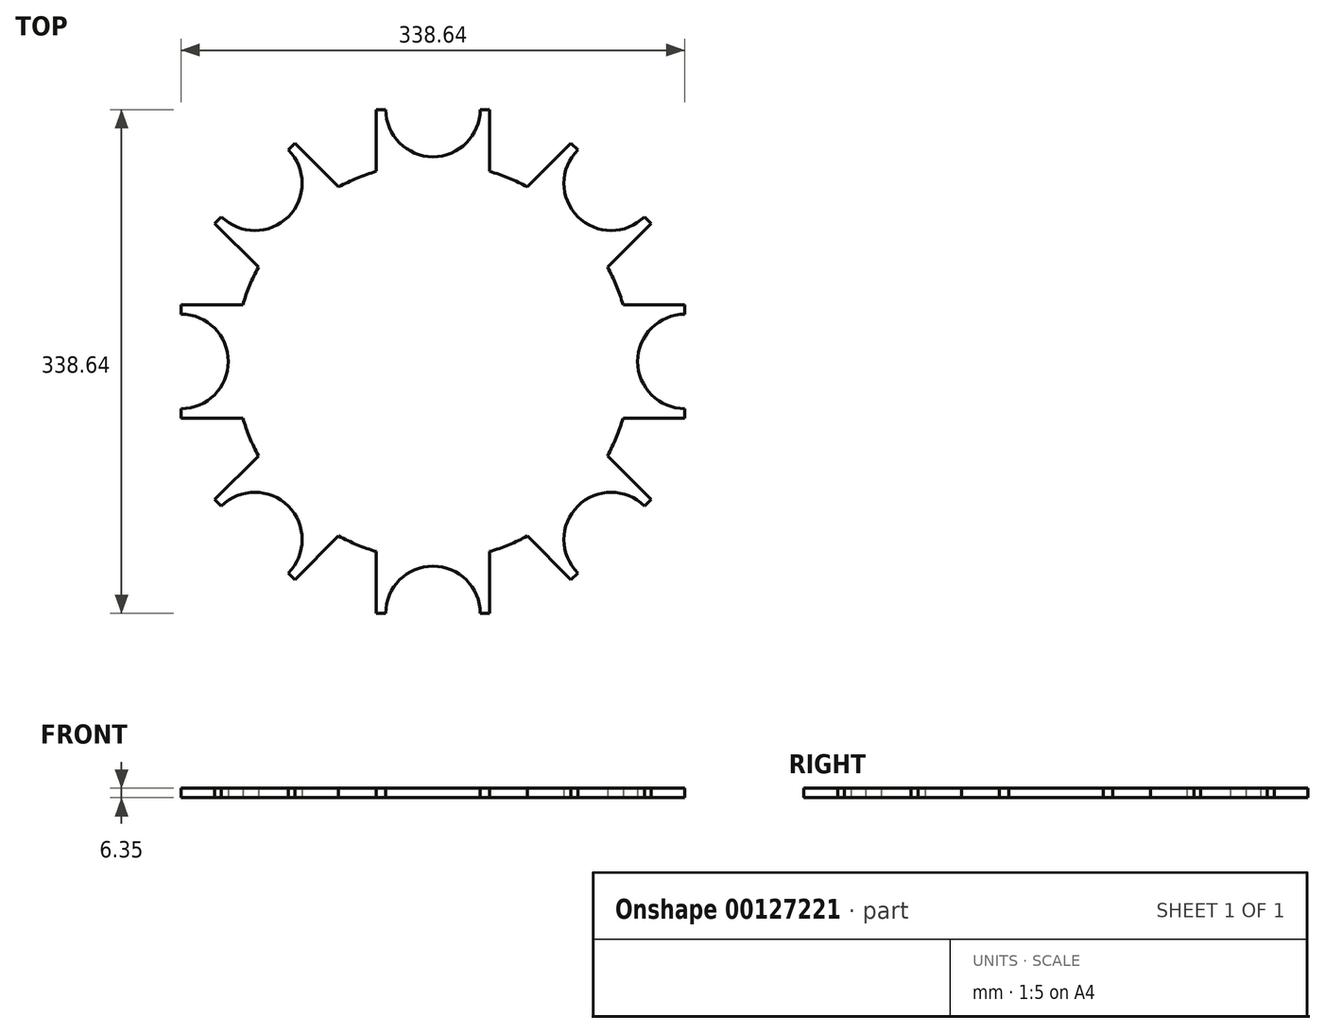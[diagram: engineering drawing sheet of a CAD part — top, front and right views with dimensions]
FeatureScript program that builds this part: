
annotation { "Feature Type Name" : "Feature", "Feature Type Description" : "" }
export const myFeature = defineFeature(function(context is Context, id is Id, definition is map)
    precondition{}
    {
        {
            var Q0;
            Q0=qCreatedBy(makeId("Top.planeOp"),FACE);
            var sketch = newSketch(context, id + "F0", { "sketchPlane" : qUnion([Q0])});
            skCircle(sketch, "E0", {"center": v(0, 0) * mm, "radius": 133.35 * mm});
            skSolve(sketch);
        }
        {
            var Q0;
            Q0=qCreatedBy(makeId("Top.planeOp"),FACE);
            var sketch = newSketch(context, id + "F1", { "sketchPlane" : qUnion([Q0])});
            skArc(sketch, "E1.0", {"start": v(-169.32, -31.75) * mm, "mid": v(-137.57, 0) * mm, "end": v(-169.32, 31.75) * mm});
            skLineSegment(sketch, "E2", {"start": v(-169.32, 31.75) * mm, "end": v(-169.32, 38.1) * mm});
            skLineSegment(sketch, "E3", {"start": v(-169.32, 38.1) * mm, "end": v(-127.8, 38.1) * mm});
            skLineSegment(sketch, "E4", {"start": v(-127.8, -38.1) * mm, "end": v(-169.32, -38.1) * mm});
            skLineSegment(sketch, "E5", {"start": v(-169.32, -38.1) * mm, "end": v(-169.32, -31.75) * mm});
            skCircle(sketch, "E6.0", {"center": v(0, 0) * mm, "radius": 133.35 * mm});
            skLineSegment(sketch, "E7", {"start": v(-137.57, 0) * mm, "end": v(0, 0) * mm, "construction": true});
            skPoint(sketch, "E7.endSnap0", {"position": v(-121.06, 0) * mm});
            skPoint(sketch, "E8.orphan", {"position": v(-121.06, 38.1) * mm});
            skPoint(sketch, "E9.orphan", {"position": v(-121.06, -38.1) * mm});
            skLineSegment(sketch, "E10.1.0", {"start": v(-146.67, -92.78) * mm, "end": v(-117.3, -63.42) * mm});
            skLineSegment(sketch, "E10.1.1", {"start": v(-142.17, -97.27) * mm, "end": v(-146.67, -92.78) * mm});
            skArc(sketch, "E10.1.2", {"start": v(-97.27, -142.17) * mm, "mid": v(-97.27, -97.27) * mm, "end": v(-142.17, -97.27) * mm});
            skLineSegment(sketch, "E10.1.3", {"start": v(-63.42, -117.3) * mm, "end": v(-92.78, -146.67) * mm});
            skLineSegment(sketch, "E10.1.4", {"start": v(-92.78, -146.67) * mm, "end": v(-97.27, -142.17) * mm});
            skLineSegment(sketch, "E10.2.0", {"start": v(-38.1, -169.32) * mm, "end": v(-38.1, -127.8) * mm});
            skLineSegment(sketch, "E10.2.1", {"start": v(-31.75, -169.32) * mm, "end": v(-38.1, -169.32) * mm});
            skArc(sketch, "E10.2.2", {"start": v(31.75, -169.32) * mm, "mid": v(0, -137.57) * mm, "end": v(-31.75, -169.32) * mm});
            skLineSegment(sketch, "E10.2.3", {"start": v(38.1, -127.8) * mm, "end": v(38.1, -169.32) * mm});
            skLineSegment(sketch, "E10.2.4", {"start": v(38.1, -169.32) * mm, "end": v(31.75, -169.32) * mm});
            skLineSegment(sketch, "E10.3.0", {"start": v(92.78, -146.67) * mm, "end": v(63.42, -117.3) * mm});
            skLineSegment(sketch, "E10.3.1", {"start": v(97.27, -142.17) * mm, "end": v(92.78, -146.67) * mm});
            skArc(sketch, "E10.3.2", {"start": v(142.17, -97.27) * mm, "mid": v(97.27, -97.27) * mm, "end": v(97.27, -142.17) * mm});
            skLineSegment(sketch, "E10.3.3", {"start": v(117.3, -63.42) * mm, "end": v(146.67, -92.78) * mm});
            skLineSegment(sketch, "E10.3.4", {"start": v(146.67, -92.78) * mm, "end": v(142.17, -97.27) * mm});
            skLineSegment(sketch, "E10.4.0", {"start": v(169.32, -38.1) * mm, "end": v(127.8, -38.1) * mm});
            skLineSegment(sketch, "E10.4.1", {"start": v(169.32, -31.75) * mm, "end": v(169.32, -38.1) * mm});
            skArc(sketch, "E10.4.2", {"start": v(169.32, 31.75) * mm, "mid": v(137.57, 0) * mm, "end": v(169.32, -31.75) * mm});
            skLineSegment(sketch, "E10.4.3", {"start": v(127.8, 38.1) * mm, "end": v(169.32, 38.1) * mm});
            skLineSegment(sketch, "E10.4.4", {"start": v(169.32, 38.1) * mm, "end": v(169.32, 31.75) * mm});
            skLineSegment(sketch, "E10.5.0", {"start": v(146.67, 92.78) * mm, "end": v(117.3, 63.42) * mm});
            skLineSegment(sketch, "E10.5.1", {"start": v(142.17, 97.27) * mm, "end": v(146.67, 92.78) * mm});
            skArc(sketch, "E10.5.2", {"start": v(97.27, 142.17) * mm, "mid": v(97.27, 97.27) * mm, "end": v(142.17, 97.27) * mm});
            skLineSegment(sketch, "E10.5.3", {"start": v(63.42, 117.3) * mm, "end": v(92.78, 146.67) * mm});
            skLineSegment(sketch, "E10.5.4", {"start": v(92.78, 146.67) * mm, "end": v(97.27, 142.17) * mm});
            skLineSegment(sketch, "E10.6.0", {"start": v(38.1, 169.32) * mm, "end": v(38.1, 127.8) * mm});
            skLineSegment(sketch, "E10.6.1", {"start": v(31.75, 169.32) * mm, "end": v(38.1, 169.32) * mm});
            skArc(sketch, "E10.6.2", {"start": v(-31.75, 169.32) * mm, "mid": v(0, 137.57) * mm, "end": v(31.75, 169.32) * mm});
            skLineSegment(sketch, "E10.6.3", {"start": v(-38.1, 127.8) * mm, "end": v(-38.1, 169.32) * mm});
            skLineSegment(sketch, "E10.6.4", {"start": v(-38.1, 169.32) * mm, "end": v(-31.75, 169.32) * mm});
            skLineSegment(sketch, "E10.7.0", {"start": v(-92.78, 146.67) * mm, "end": v(-63.42, 117.3) * mm});
            skLineSegment(sketch, "E10.7.1", {"start": v(-97.27, 142.17) * mm, "end": v(-92.78, 146.67) * mm});
            skArc(sketch, "E10.7.2", {"start": v(-142.17, 97.27) * mm, "mid": v(-97.27, 97.27) * mm, "end": v(-97.27, 142.17) * mm});
            skLineSegment(sketch, "E10.7.3", {"start": v(-117.3, 63.42) * mm, "end": v(-146.67, 92.78) * mm});
            skLineSegment(sketch, "E10.7.4", {"start": v(-146.67, 92.78) * mm, "end": v(-142.17, 97.27) * mm});
            skSolve(sketch);
        }
        {
            var Q0;
            Q0=makeQuery(id+"F1.imprint","IMPRINT",FACE,{"disambiguationData":[TD([[makeQuery(id+"F1.imprint","IMPRINT",EDGE,{"derivedFrom":sQuery(id+"F1.wireOp",EDGE,"E1.0")}),-1.0]])]});
            var Q1;
            {var subQ0=sQuery(id+"F1.wireOp",EDGE,"E10.1.0");Q1=makeQuery(id+"F1.imprint","IMPRINT",FACE,{"disambiguationData":[TD([[makeQuery(id+"F1.imprint","IMPRINT",EDGE,{"derivedFrom":subQ0}),-1.0]])]});}
            var Q2;
            {var subQ0=sQuery(id+"F1.wireOp",EDGE,"E10.2.0");Q2=makeQuery(id+"F1.imprint","IMPRINT",FACE,{"disambiguationData":[TD([[makeQuery(id+"F1.imprint","IMPRINT",EDGE,{"derivedFrom":subQ0}),-1.0]])]});}
            var Q3;
            {var subQ0=sQuery(id+"F1.wireOp",EDGE,"E10.3.0");Q3=makeQuery(id+"F1.imprint","IMPRINT",FACE,{"disambiguationData":[TD([[makeQuery(id+"F1.imprint","IMPRINT",EDGE,{"derivedFrom":subQ0}),-1.0]])]});}
            var Q4;
            {var subQ0=sQuery(id+"F1.wireOp",EDGE,"E10.4.0");Q4=makeQuery(id+"F1.imprint","IMPRINT",FACE,{"disambiguationData":[TD([[makeQuery(id+"F1.imprint","IMPRINT",EDGE,{"derivedFrom":subQ0}),-1.0]])]});}
            var Q5;
            {var subQ0=sQuery(id+"F1.wireOp",EDGE,"E10.5.0");Q5=makeQuery(id+"F1.imprint","IMPRINT",FACE,{"disambiguationData":[TD([[makeQuery(id+"F1.imprint","IMPRINT",EDGE,{"derivedFrom":subQ0}),-1.0]])]});}
            var Q6;
            {var subQ0=sQuery(id+"F1.wireOp",EDGE,"E10.6.0");Q6=makeQuery(id+"F1.imprint","IMPRINT",FACE,{"disambiguationData":[TD([[makeQuery(id+"F1.imprint","IMPRINT",EDGE,{"derivedFrom":subQ0}),-1.0]])]});}
            var Q7;
            {var subQ0=sQuery(id+"F1.wireOp",EDGE,"E10.7.0");Q7=makeQuery(id+"F1.imprint","IMPRINT",FACE,{"disambiguationData":[TD([[makeQuery(id+"F1.imprint","IMPRINT",EDGE,{"derivedFrom":subQ0}),-1.0]])]});}
            var Q8;
            {var subQ0=sQuery(id+"F1.wireOp",EDGE,"E6.0");var subQ10=makeQuery(id+"F1.imprint","INTERSECT",VERTEX,{"derivedFrom":[subQ0,sQuery(id+"F1.wireOp",EDGE,"E10.4.3")]});Q8=makeQuery(id+"F1.imprint","IMPRINT",FACE,{"disambiguationData":[TD([[makeQuery(id+"F1.imprint","IMPRINT",EDGE,{"disambiguationData":[TD([[subQ10,-1.0]])],"derivedFrom":subQ0}),1.0]])]});}
            extrude(context, id + "F2", {"entities" : qUnion([Q0, Q1, Q2, Q3, Q4, Q5, Q6, Q7, Q8]), "depth" : 6.35 * mm});
        }
    });
